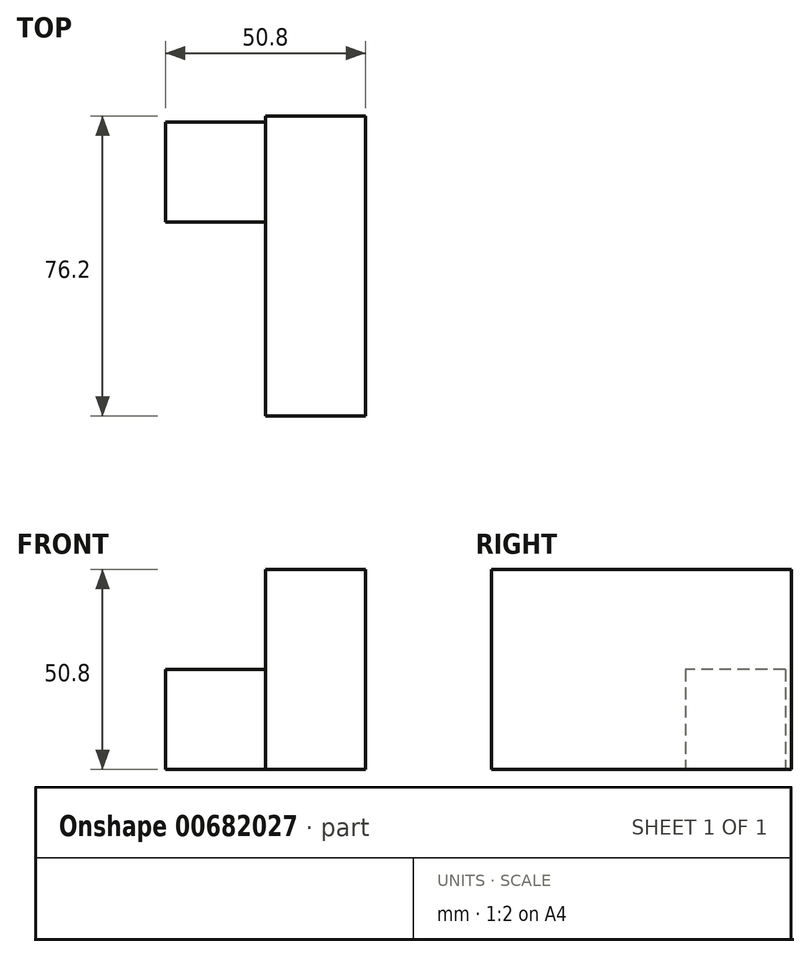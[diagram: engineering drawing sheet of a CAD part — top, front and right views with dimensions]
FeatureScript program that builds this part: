
annotation { "Feature Type Name" : "Feature", "Feature Type Description" : "" }
export const myFeature = defineFeature(function(context is Context, id is Id, definition is map)
    precondition{}
    {
        {
            var Q0;
            Q0=qCreatedBy(makeId("Front.planeOp"),FACE);
            var sketch = newSketch(context, id + "F0", { "sketchPlane" : qUnion([Q0])});
            skLineSegment(sketch, "E0.bottom", {"start": v(25.4, 35.63) * mm, "end": v(0, 35.63) * mm});
            skLineSegment(sketch, "E0.top", {"start": v(25.4, -15.17) * mm, "end": v(0, -15.17) * mm});
            skLineSegment(sketch, "E0.left", {"start": v(25.4, 35.63) * mm, "end": v(25.4, -15.17) * mm});
            skLineSegment(sketch, "E0.right", {"start": v(0, 35.63) * mm, "end": v(0, -15.17) * mm});
            skSolve(sketch);
        }
        {
            var Q0;
            Q0 = qSketchRegion(id + "F0", true);
            extrude(context, id + "F1", {"entities" : qUnion([Q0]), "depth" : 76.2 * mm, "offsetDistance" : 25.4 * mm});
        }
        {
            var Q0;
            Q0=makeQuery(id+"F1.opExtrude","SWEPT_FACE",FACE,{"disambiguationData":[OSD([sQuery(id+"F0.wireOp",EDGE,"E0.right")])]});
            var sketch = newSketch(context, id + "F2", { "sketchPlane" : qUnion([Q0])});
            skLineSegment(sketch, "E1.bottom", {"start": v(1.52, 10.23) * mm, "end": v(26.92, 10.23) * mm});
            skLineSegment(sketch, "E1.top", {"start": v(1.52, -15.17) * mm, "end": v(26.92, -15.17) * mm});
            skLineSegment(sketch, "E1.left", {"start": v(1.52, 10.23) * mm, "end": v(1.52, -15.17) * mm});
            skLineSegment(sketch, "E1.right", {"start": v(26.92, 10.23) * mm, "end": v(26.92, -15.17) * mm});
            skSolve(sketch);
        }
        {
            var Q0;
            Q0 = qSketchRegion(id + "F2", true);
            extrude(context, id + "F3", {"entities" : qUnion([Q0]), "operationType" : NewBodyOperationType.ADD, "depth" : 25.4 * mm, "offsetDistance" : 25.4 * mm});
        }
    });
